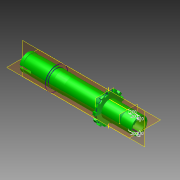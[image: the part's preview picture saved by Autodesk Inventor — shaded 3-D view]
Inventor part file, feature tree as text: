
AUTODESK INVENTOR PART (.ipt)
format: ipt  version: 2015 (Build 190159000, 159)  size: 349,696 bytes
history: native  units: in
note: dims shown in document units (in); Inventor stores cm internally (conversion verified against a paired STEP export)
features: sketch x10, extrude x9, revolve x4, hole x2, plane x2, chamfer x2, mirror x1, pattern_circular x1
ambient origin geometry x8: Origin, YZ Plane, XZ Plane, XY Plane, X Axis, Y Axis, Z Axis, Center Point
bodies: Solid1 (feature_tree)
feature tree (31):
  revolve  "Revolution1"  [1 undecoded]
  extrude  "Extrusion1"  Depth=0.29in
  hole  "Hole1"  [1 undecoded]
  hole  "Hole2"  [1 undecoded]
  sketch  "Sketch3"  dims[d4=0.3in d5=0.1in]
  extrude  "Extrusion2"  Depth=0.44in
  extrude  "Extrusion3"  Depth=0.05in
  extrude  "Extrusion4"  Depth=0.04in
  mirror  "Mirror1"
  plane  "Work Plane2"
  sketch  "Sketch7"  dims[d8=0.3in d9=0.44in]
  extrude  "Extrusion5"  Depth=1.0in TaperAngle=0.0deg
  extrude  "Extrusion6"  Depth=1.0in
  pattern_circular  "Circular Pattern1"  [2 undecoded]
  plane  "Work Plane3"
  extrude  "Extrusion7"  Depth=0.125in TaperAngle=0.0deg
  sketch  "Sketch9"  dims[d12=90.0deg d13=0.04in]
  revolve  "Revolution3"  [1 undecoded]
  revolve  "Revolution4"  [1 undecoded]
  revolve  "Revolution5"  [1 undecoded]
  extrude  "Extrusion8"  Depth=0.025in
  chamfer  "Chamfer1"  Distance=0.025in
  extrude  "Extrusion9"  Depth=0.01in
  chamfer  "Chamfer2"  Distance=0.03in
  sketch  "Sketch1"  dims[d0=0.07in d1=0.4in]
  sketch  "Sketch2"  dims[d2=0.365in d3=0.29in]
  sketch  "Sketch4"  dims[d6=0.06in d7=0.3in]
  sketch  "Sketch8"  dims[d10=0.28in d11=0.05in]
  sketch  "Sketch10"  dims[d14=0.2in d15=1.0in d16=0.0in]
  sketch  "Sketch14"  dims[d17=1.0in d18=1.0in]
  sketch  "Sketch15"  dims[d19=0.1875in d20=0.75in d21=0.25in d22=0.25in d23=0.5635in d24=0.4375in d25=0.0in d26=1.0in d27=1.0in d28=0.1875in d29=0.75in d30=0.25in d31=0.05in d32=0.5635in d33=0.375in d34=0.0in d35=0.07in d36=0.0in d37=0.085in d38=0.0in d39=1.15in d40=0.0in d42=-1.44in d43=0.45in d44=0.025in d45=0.025in d46=0.01in d47=0.03in d48=0.05in d49=0.0in d50=0.05in d51=0.0in d52=5.1181in d53=360.0deg d55=-1.8in d56=1.0in d57=0.0in d58=0.2in d59=0.2in d62=0.02in d63=0.02in d64=0.2in d65=60.0deg d66=60.0deg d69=0.02in d70=0.1in d71=0.2in d72=0.0in d73=60.0deg d74=0.005in d75=0.0in d76=0.005in d77=0.125in d78=45.0deg d79=0.005in d80=0.005in d81=0.005in d82=0.0in d83=0.005in d84=0.125in d85=45.0deg]
note: 8 required parameter values undecoded (feature->parameter linkage not recoverable at this tier; creation-order binding heuristic only, values carry confidence <= 0.55)